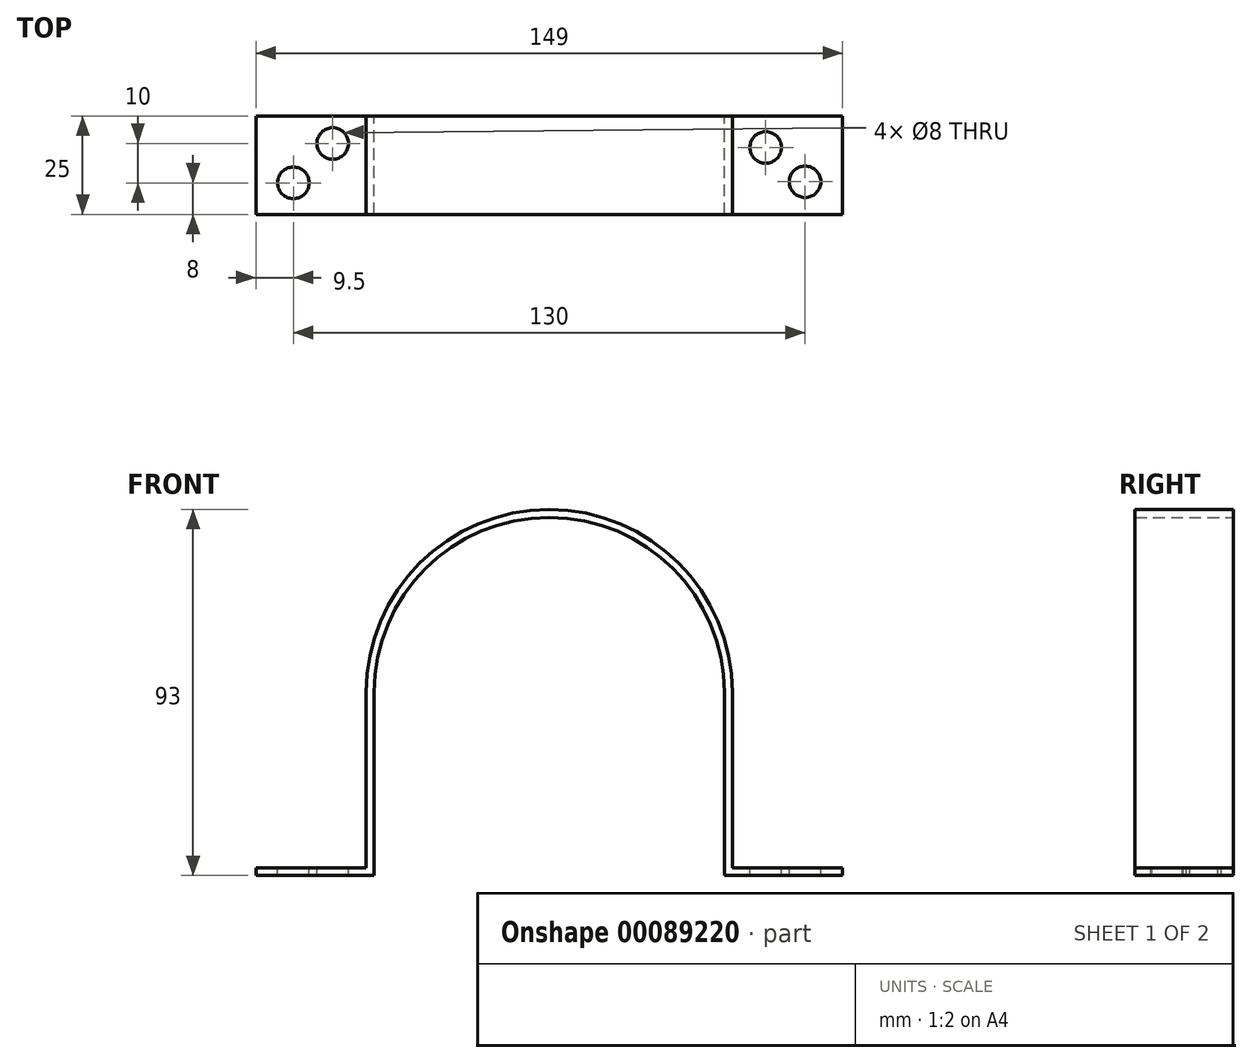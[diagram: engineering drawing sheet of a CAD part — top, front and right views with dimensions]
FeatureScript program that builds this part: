
annotation { "Feature Type Name" : "Feature", "Feature Type Description" : "" }
export const myFeature = defineFeature(function(context is Context, id is Id, definition is map)
    precondition{}
    {
        {
            var Q0;
            Q0=qCreatedBy(makeId("Front.planeOp"),FACE);
            var sketch = newSketch(context, id + "F0", { "sketchPlane" : qUnion([Q0])});
            skArc(sketch, "E0", {"start": v(44.5, 0) * mm, "mid": v(0, 44.5) * mm, "end": v(-44.5, 0) * mm});
            skArc(sketch, "E1", {"start": v(46.5, 0) * mm, "mid": v(0, 46.5) * mm, "end": v(-46.5, 0) * mm});
            skLineSegment(sketch, "E2", {"start": v(-74.5, -46.5) * mm, "end": v(-44.5, -46.5) * mm});
            skLineSegment(sketch, "E3", {"start": v(-46.5, 0) * mm, "end": v(-46.5, -44.5) * mm});
            skLineSegment(sketch, "E4", {"start": v(-44.5, 0) * mm, "end": v(-44.5, -46.5) * mm});
            skLineSegment(sketch, "E5", {"start": v(44.5, 0) * mm, "end": v(44.5, -46.5) * mm});
            skLineSegment(sketch, "E6", {"start": v(46.5, 0) * mm, "end": v(46.5, -44.5) * mm});
            skLineSegment(sketch, "E7", {"start": v(-46.5, -44.5) * mm, "end": v(-74.5, -44.5) * mm});
            skLineSegment(sketch, "E8", {"start": v(-74.5, -44.5) * mm, "end": v(-74.5, -46.5) * mm});
            skLineSegment(sketch, "E9", {"start": v(46.5, -44.5) * mm, "end": v(74.5, -44.5) * mm});
            skLineSegment(sketch, "E10", {"start": v(74.5, -44.5) * mm, "end": v(74.5, -46.5) * mm});
            skLineSegment(sketch, "E11.trimOffspring", {"start": v(44.5, -46.5) * mm, "end": v(74.5, -46.5) * mm});
            skSolve(sketch);
        }
        {
            var Q0;
            Q0 = qSketchRegion(id + "F0", true);
            extrude(context, id + "F1", {"entities" : qUnion([Q0]), "depth" : 25 * mm});
        }
        {
            var Q0;
            Q0=makeQuery(id+"F1.opExtrude","SWEPT_FACE",FACE,{"disambiguationData":[OSD([sQuery(id+"F0.wireOp",EDGE,"E9")])]});
            var sketch = newSketch(context, id + "F2", { "sketchPlane" : qUnion([Q0])});
            skCircle(sketch, "E12", {"center": v(55, -8) * mm, "radius": 4 * mm});
            skCircle(sketch, "E13", {"center": v(65, -16.73) * mm, "radius": 4 * mm});
            skCircle(sketch, "E14", {"center": v(-55, -7) * mm, "radius": 4 * mm});
            skCircle(sketch, "E15", {"center": v(-65, -17) * mm, "radius": 4 * mm});
            skSolve(sketch);
        }
        {
            var Q0;
            Q0=makeQuery(id+"F2.imprint","IMPRINT",FACE,{"disambiguationData":[TD([[makeQuery(id+"F2.imprint","IMPRINT",EDGE,{"derivedFrom":sQuery(id+"F2.wireOp",EDGE,"E15")}),1.0]])]});
            var Q1;
            Q1=makeQuery(id+"F2.imprint","IMPRINT",FACE,{"disambiguationData":[TD([[makeQuery(id+"F2.imprint","IMPRINT",EDGE,{"derivedFrom":sQuery(id+"F2.wireOp",EDGE,"E14")}),1.0]])]});
            var Q2;
            Q2=makeQuery(id+"F2.imprint","IMPRINT",FACE,{"disambiguationData":[TD([[makeQuery(id+"F2.imprint","IMPRINT",EDGE,{"derivedFrom":sQuery(id+"F2.wireOp",EDGE,"E12")}),1.0]])]});
            var Q3;
            Q3=makeQuery(id+"F2.imprint","IMPRINT",FACE,{"disambiguationData":[TD([[makeQuery(id+"F2.imprint","IMPRINT",EDGE,{"derivedFrom":sQuery(id+"F2.wireOp",EDGE,"E13")}),1.0]])]});
            extrude(context, id + "F3", {"entities" : qUnion([Q0, Q1, Q2, Q3]), "operationType" : NewBodyOperationType.REMOVE, "endBound" : BoundingType.THROUGH_ALL, "oppositeDirection" : true, "depth" : 25 * mm});
        }
    });
